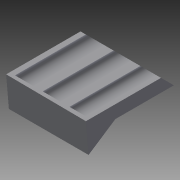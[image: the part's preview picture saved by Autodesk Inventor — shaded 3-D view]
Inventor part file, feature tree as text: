
AUTODESK INVENTOR PART (.ipt)
format: ipt  version: 2015 (Build 190159000, 159)  size: 241,152 bytes
history: native  units: mm
features: sketch x8, projected_geometry x5, plane x2, loft x2, split x1
ambient origin geometry x8: Origin, YZ Plane, XZ Plane, XY Plane, X Axis, Y Axis, Z Axis, Center Point
bodies: Body1 (feature_tree)
feature tree (18):
  sketch  "Sketch1"  dims[d0=29.0mm d1=27.5mm]
  sketch  "Sketch4"  dims[d2=25.0mm d3=22.25mm]
  plane  "Work Plane4"
  loft  "Loft1"
  sketch  "Sketch7"  dims[d6=38.25mm]
  loft  "Loft3"
  split  "Split1"
  plane  "Work Plane3"
  sketch  "Sketch5"  dims[d4=20.0mm]
  sketch  "Sketch6"  dims[d5=19.0mm]
  projected_geometry  "Projected Loop2"
  sketch  "Sketch10"  dims[d7=36.25mm]
  projected_geometry  "Projected Loop4"
  sketch  "Sketch11"  dims[d8=33.625mm]
  projected_geometry  "Projected Loop5"
  sketch  "Sketch13"  dims[d9=31.125mm d10=29.5mm d11=0.0mm d12=0.0mm d13=0.0mm d14=0.0mm d15=0.0mm d20=20.0mm d22=20.0mm d23=20.0mm d24=7.0mm d25=4.586mm d51=45.0deg d53=0.0mm d55=29.903294mm d56=29.0mm d57=27.5mm d58=25.0mm d59=22.25mm d60=20.0mm d61=19.0mm d62=38.25mm d63=36.25mm d64=33.625mm d65=31.125mm d66=29.5mm d67=0.0mm d68=0.0mm d69=0.0mm d70=0.0mm d71=0.0mm d72=20.0mm d73=20.0mm d74=20.0mm d75=7.0mm d76=4.586mm d77=29.0mm d78=27.5mm d79=25.0mm d80=22.25mm d81=20.0mm d82=19.0mm d83=38.25mm d84=36.25mm d85=33.625mm d86=31.125mm d87=29.5mm d88=0.0mm d89=0.0mm d90=0.0mm d91=0.0mm d92=0.0mm d93=20.0mm d94=20.0mm d95=20.0mm d96=7.0mm d97=4.586mm d98=100.0mm d99=0.0mm d100=90.0deg d101=0.0mm d102=90.0deg d106=5.0mm d111=14.835299mm d113=25.0mm d114=40.0mm d115=25.0mm d116=40.0mm d117=0.0mm d118=90.0deg d119=0.0mm d120=90.0deg d122=18.0mm]
  projected_geometry  "Projected Loop6"
  projected_geometry  "Projected Loop7"
